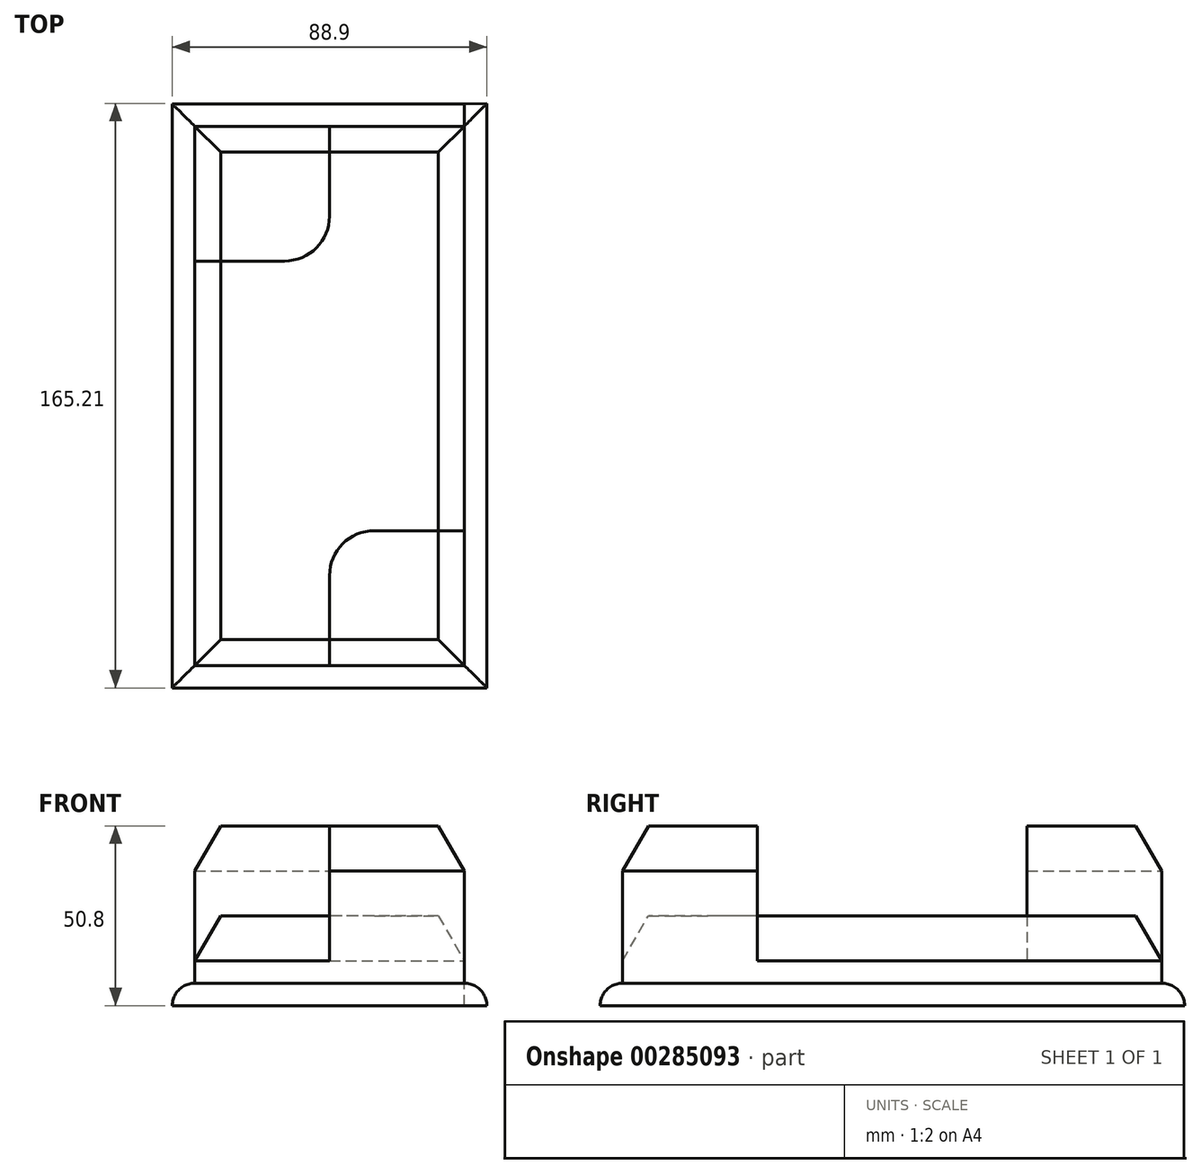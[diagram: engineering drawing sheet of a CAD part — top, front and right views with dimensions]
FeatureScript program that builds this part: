
annotation { "Feature Type Name" : "Feature", "Feature Type Description" : "" }
export const myFeature = defineFeature(function(context is Context, id is Id, definition is map)
    precondition{}
    {
        {
            var Q0;
            Q0=qCreatedBy(makeId("Top.planeOp"),FACE);
            var sketch = newSketch(context, id + "F0", { "sketchPlane" : qUnion([Q0])});
            skLineSegment(sketch, "E0", {"start": v(0, 69.18) * mm, "end": v(76.2, 69.18) * mm});
            skLineSegment(sketch, "E1", {"start": v(76.2, 69.18) * mm, "end": v(76.2, -83.22) * mm});
            skLineSegment(sketch, "E2", {"start": v(76.2, -83.22) * mm, "end": v(0, -83.22) * mm});
            skLineSegment(sketch, "E3", {"start": v(0, -83.22) * mm, "end": v(0, 69.18) * mm});
            skLineSegment(sketch, "E4.0", {"start": v(0, 75.53) * mm, "end": v(76.2, 75.53) * mm});
            skLineSegment(sketch, "E5.0", {"start": v(76.2, -89.57) * mm, "end": v(0, -89.57) * mm});
            skLineSegment(sketch, "E6.0", {"start": v(-6.35, -83.22) * mm, "end": v(-6.35, 69.18) * mm});
            skLineSegment(sketch, "E7.0", {"start": v(82.55, 69.18) * mm, "end": v(82.55, -83.22) * mm});
            skLineSegment(sketch, "E8", {"start": v(-6.35, 69.18) * mm, "end": v(-6.35, 75.53) * mm});
            skLineSegment(sketch, "E9", {"start": v(0, 75.53) * mm, "end": v(-6.35, 75.53) * mm});
            skLineSegment(sketch, "E10", {"start": v(82.55, 69.18) * mm, "end": v(82.55, 75.64) * mm});
            skLineSegment(sketch, "E11", {"start": v(76.2, 75.53) * mm, "end": v(82.55, 75.64) * mm});
            skLineSegment(sketch, "E12", {"start": v(-6.35, -83.22) * mm, "end": v(-6.35, -89.57) * mm});
            skLineSegment(sketch, "E13", {"start": v(-6.35, -89.57) * mm, "end": v(82.55, -89.57) * mm});
            skLineSegment(sketch, "E14", {"start": v(82.55, -83.22) * mm, "end": v(82.55, -89.57) * mm});
            skPoint(sketch, "E15.orphan", {"position": v(-17.31, -89.57) * mm});
            skLineSegment(sketch, "E16", {"start": v(38.1, -83.22) * mm, "end": v(38.1, -57.82) * mm});
            skLineSegment(sketch, "E17", {"start": v(50.8, -45.12) * mm, "end": v(76.2, -45.12) * mm});
            skPoint(sketch, "E18.visualSharp", {"position": v(38.1, -45.12) * mm});
            skArc(sketch, "E18.filletArc", {"start": v(50.8, -45.12) * mm, "mid": v(41.82, -48.84) * mm, "end": v(38.1, -57.82) * mm});
            skLineSegment(sketch, "E19", {"start": v(38.1, 69.18) * mm, "end": v(38.1, 43.78) * mm});
            skLineSegment(sketch, "E20", {"start": v(25.4, 31.08) * mm, "end": v(0, 31.08) * mm});
            skArc(sketch, "E21.filletArc", {"start": v(25.4, 31.08) * mm, "mid": v(34.38, 34.8) * mm, "end": v(38.1, 43.78) * mm});
            skSolve(sketch);
        }
        {
            var Q0;
            Q0=makeQuery(id+"F0.imprint","IMPRINT",FACE,{"disambiguationData":[TD([[makeQuery(id+"F0.imprint","IMPRINT",EDGE,{"derivedFrom":sQuery(id+"F0.wireOp",EDGE,"E4.0")}),-1.0]])]});
            extrude(context, id + "F1", {"entities" : qUnion([Q0]), "depth" : 6.35 * mm});
        }
        {
            var Q0;
            {var subQ3=sQuery(id+"F0.wireOp",EDGE,"E16");Q0=makeQuery(id+"F0.imprint","IMPRINT",FACE,{"disambiguationData":[TD([[makeQuery(id+"F0.imprint","IMPRINT",EDGE,{"derivedFrom":subQ3}),1.0]])]});}
            extrude(context, id + "F2", {"entities" : qUnion([Q0]), "operationType" : NewBodyOperationType.ADD, "depth" : 25.4 * mm});
        }
        {
            var Q0;
            {var subQ4=sQuery(id+"F0.wireOp",EDGE,"E16");Q0=makeQuery(id+"F0.imprint","IMPRINT",FACE,{"disambiguationData":[TD([[makeQuery(id+"F0.imprint","IMPRINT",EDGE,{"derivedFrom":subQ4}),-1.0]])]});}
            var Q1;
            {var subQ0=sQuery(id+"F0.wireOp",EDGE,"E19");Q1=makeQuery(id+"F0.imprint","IMPRINT",FACE,{"disambiguationData":[TD([[makeQuery(id+"F0.imprint","IMPRINT",EDGE,{"derivedFrom":subQ0}),-1.0]])]});}
            extrude(context, id + "F3", {"entities" : qUnion([Q0, Q1]), "operationType" : NewBodyOperationType.ADD, "depth" : 50.8 * mm});
        }
        {
            var Q0;
            Q0=makeQuery(id+"F1.opExtrude","CAP_EDGE",EDGE,{"disambiguationData":[OSD([sQuery(id+"F0.wireOp",EDGE,"E7.0"),sQuery(id+"F0.wireOp",EDGE,"E10"),sQuery(id+"F0.wireOp",EDGE,"E14")])],"isStart":false});
            var Q1;
            Q1=makeQuery(id+"F1.opExtrude","CAP_EDGE",EDGE,{"disambiguationData":[OSD([sQuery(id+"F0.wireOp",EDGE,"E4.0"),sQuery(id+"F0.wireOp",EDGE,"E9")])],"isStart":false});
            var Q2;
            Q2=makeQuery(id+"F1.opExtrude","CAP_EDGE",EDGE,{"disambiguationData":[OSD([sQuery(id+"F0.wireOp",EDGE,"E11")])],"isStart":false});
            var Q3;
            Q3=makeQuery(id+"F1.opExtrude","CAP_EDGE",EDGE,{"disambiguationData":[OSD([sQuery(id+"F0.wireOp",EDGE,"E13")])],"isStart":false});
            var Q4;
            Q4=makeQuery(id+"F1.opExtrude","CAP_EDGE",EDGE,{"disambiguationData":[OSD([sQuery(id+"F0.wireOp",EDGE,"E6.0"),sQuery(id+"F0.wireOp",EDGE,"E8"),sQuery(id+"F0.wireOp",EDGE,"E12")])],"isStart":false});
            fillet(context, id + "F4", {"entities" : qUnion([Q0, Q1, Q2, Q3, Q4]), "radius" : 6.35 * mm, "tangentPropagation" : true, "allowEdgeOverflow" : false});
        }
        {
            var Q0;
            Q0=makeQuery(id+"F2.opExtrude","CAP_EDGE",EDGE,{"disambiguationData":[OSD([sQuery(id+"F0.wireOp",EDGE,"E3")])],"isStart":false});
            var Q1;
            Q1=makeQuery(id+"F2.opExtrude","CAP_EDGE",EDGE,{"disambiguationData":[OSD([sQuery(id+"F0.wireOp",EDGE,"E2")])],"isStart":false});
            var Q2;
            Q2=makeQuery(id+"F3.opExtrude","CAP_EDGE",EDGE,{"disambiguationData":[OSD([sQuery(id+"F0.wireOp",EDGE,"E2")])],"isStart":false});
            var Q3;
            Q3=makeQuery(id+"F3.opExtrude","CAP_EDGE",EDGE,{"disambiguationData":[OSD([sQuery(id+"F0.wireOp",EDGE,"E3")])],"isStart":false});
            var Q4;
            Q4=makeQuery(id+"F3.opExtrude","CAP_EDGE",EDGE,{"disambiguationData":[OSD([sQuery(id+"F0.wireOp",EDGE,"E1")])],"isStart":false});
            var Q5;
            Q5=makeQuery(id+"F3.opExtrude","CAP_EDGE",EDGE,{"disambiguationData":[OSD([sQuery(id+"F0.wireOp",EDGE,"E0")])],"isStart":false});
            var Q6;
            Q6=makeQuery(id+"F2.opExtrude","CAP_EDGE",EDGE,{"disambiguationData":[OSD([sQuery(id+"F0.wireOp",EDGE,"E1")])],"isStart":false});
            var Q7;
            Q7=makeQuery(id+"F2.opExtrude","CAP_EDGE",EDGE,{"disambiguationData":[OSD([sQuery(id+"F0.wireOp",EDGE,"E0")])],"isStart":false});
            chamfer(context, id + "F5", {"entities" : qUnion([Q0, Q1, Q2, Q3, Q4, Q5, Q6, Q7]), "chamferType" : ChamferType.OFFSET_ANGLE, "width" : 12.7 * mm, "oppositeDirection" : false, "angle" : 30 * degree, "tangentPropagation" : true});
        }
    });
